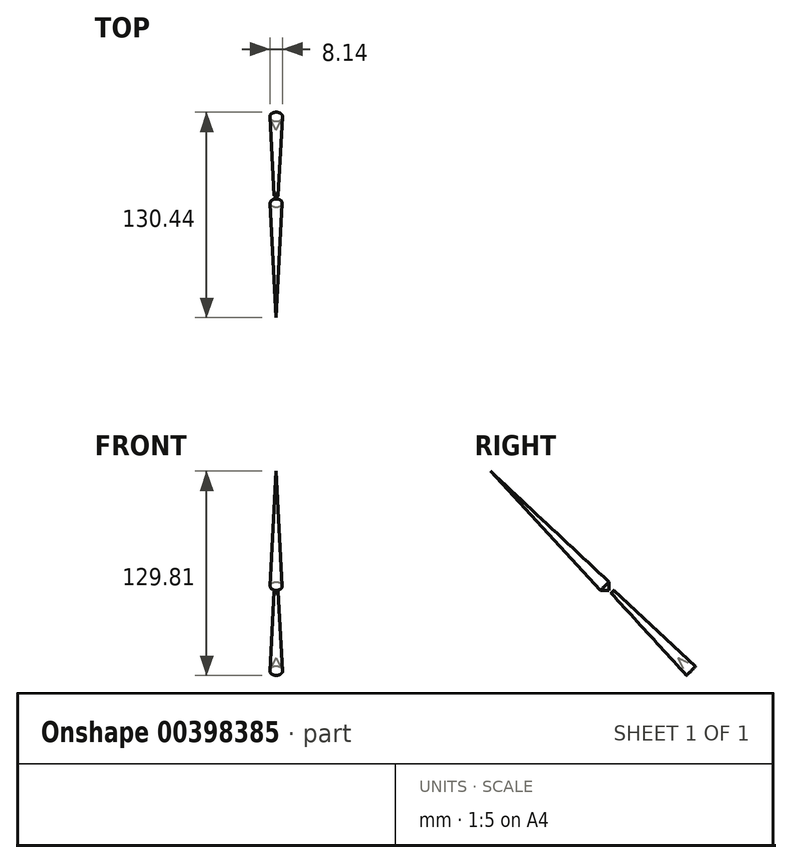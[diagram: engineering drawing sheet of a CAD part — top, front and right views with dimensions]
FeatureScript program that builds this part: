
annotation { "Feature Type Name" : "Feature", "Feature Type Description" : "" }
export const myFeature = defineFeature(function(context is Context, id is Id, definition is map)
    precondition{}
    {
        {
            var Q0;
            Q0=qCreatedBy(makeId("Right.planeOp"),FACE);
            var sketch = newSketch(context, id + "F0", { "sketchPlane" : qUnion([Q0])});
            skLineSegment(sketch, "E0", {"start": v(0, 0) * mm, "end": v(-75.33, 75.8) * mm});
            skLineSegment(sketch, "E1", {"start": v(-75.33, 75.8) * mm, "end": v(-5.38, 0) * mm});
            skLineSegment(sketch, "E2", {"start": v(-5.38, 0) * mm, "end": v(0, 0) * mm});
            skSolve(sketch);
        }
        {
            var Q0;
            Q0=makeQuery(id+"F0.imprint","IMPRINT",FACE,{"disambiguationData":[TD([[makeQuery(id+"F0.imprint","IMPRINT",EDGE,{"derivedFrom":sQuery(id+"F0.wireOp",EDGE,"E0")}),1.0]])]});
            var Q1;
            Q1=sQuery(id+"F0.wireOp",EDGE,"E0");
            revolve(context, id + "F1", {"entities" : qUnion([Q0]), "axis" : qUnion([Q1]), "revolveType" : RevolveType.FULL});
        }
        {
            var Q0;
            Q0=qCreatedBy(makeId("Right.planeOp"),FACE);
            var sketch = newSketch(context, id + "F2", { "sketchPlane" : qUnion([Q0])});
            skLineSegment(sketch, "E3", {"start": v(0, 5.51) * mm, "end": v(3.12, 0) * mm});
            skLineSegment(sketch, "E4", {"start": v(3.12, 0) * mm, "end": v(3.12, -1.74) * mm});
            skLineSegment(sketch, "E5", {"start": v(3.12, -1.74) * mm, "end": v(43.9, -42.76) * mm});
            skLineSegment(sketch, "E6", {"start": v(-5.77, 0) * mm, "end": v(3.18, -33.12) * mm});
            skLineSegment(sketch, "E7", {"start": v(-5.77, 0) * mm, "end": v(3.12, -1.74) * mm});
            skArc(sketch, "E8", {"start": v(3.18, -33.12) * mm, "mid": v(21.52, -46.46) * mm, "end": v(43.9, -42.76) * mm});
            skLineSegment(sketch, "E9", {"start": v(3.12, 0) * mm, "end": v(55.11, -48.27) * mm});
            skLineSegment(sketch, "E10", {"start": v(55.11, -48.27) * mm, "end": v(43.9, -42.76) * mm});
            skLineSegment(sketch, "E11", {"start": v(0, 5.51) * mm, "end": v(-5.77, 0) * mm});
            skSolve(sketch);
        }
        {
            var Q0;
            Q0=makeQuery(id+"F2.imprint","IMPRINT",FACE,{"disambiguationData":[TD([[makeQuery(id+"F2.imprint","IMPRINT",EDGE,{"derivedFrom":sQuery(id+"F2.wireOp",EDGE,"E4")}),1.0]])]});
            var Q1;
            Q1=sQuery(id+"F2.wireOp",EDGE,"E5");
            revolve(context, id + "F3", {"entities" : qUnion([Q0]), "axis" : qUnion([Q1]), "revolveType" : RevolveType.FULL});
        }
    });
